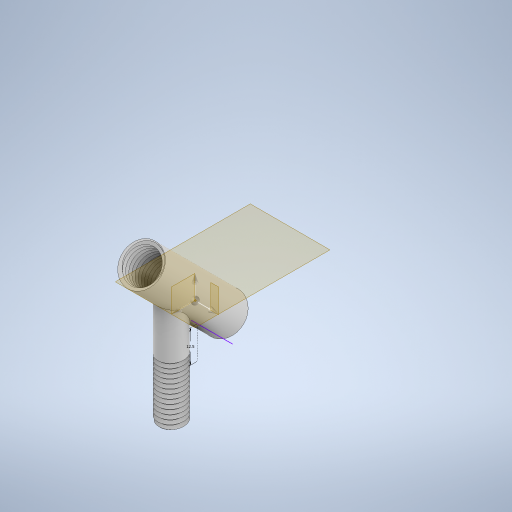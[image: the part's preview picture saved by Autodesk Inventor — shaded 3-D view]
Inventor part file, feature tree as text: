
AUTODESK INVENTOR PART (.ipt)
format: ipt  version: 2024 (Build 280153000, 153)  size: 883,200 bytes
history: native  units: mm
features: sketch x9, plane x5, extrude x3, helix x2, hole x1, chamfer x1
ambient origin geometry x8: Origin, YZ Plane, XZ Plane, XY Plane, X Axis, Y Axis, Z Axis, Center Point
bodies: Solid1 (feature_tree)
feature tree (21):
  extrude  "Extrusion1"  Depth=25.0mm TaperAngle=0.0deg
  plane  "Work Plane1"
  plane  "Work Plane3"
  sketch  "Sketch9"  dims[d16=10.0mm d17=12.5mm]
  plane  "Work Plane4"
  sketch  "Sketch10"  dims[d18=12.5mm d19=45.0deg]
  plane  "Work Plane5"
  extrude  "Extrusion4"  Depth=12.5mm
  hole  "Hole1"  [1 undecoded]
  extrude  "Extrusion5"  Depth=45.0mm TaperAngle=0.0deg
  chamfer  "Chamfer1"  Distance=25.0mm
  sketch  "Sketch14"  dims[d37=1.7mm]
  plane  "Work Plane6"
  helix  "Coil1"  [1 undecoded]
  helix  "Coil2"  [1 undecoded]
  sketch  "Sketch1"  dims[d0=10.0mm d1=25.0mm d2=0.0mm]
  sketch  "Sketch11"  dims[d20=15.0mm d21=45.0mm d22=0.0mm]
  sketch  "Sketch12"  dims[d23=12.0mm]
  sketch  "Sketch13"  dims[d24=12.0mm d25=6.0mm d26=4.0mm d27=2.0mm d28=90.0deg d29=8.0mm d30=20.594885mm d31=25.0mm d32=0.0mm d33=0.8mm d34=2.0mm d35=45.0deg d36=60.0deg]
  sketch  "Sketch15"  dims[d38=2.0mm]
  sketch  "Sketch16"  dims[d39=0.2mm d40=0.0mm d41=1.7mm d42=25.0mm d43=10.0mm d44=0.0mm d45=90.0deg d46=90.0deg d47=0.0mm d48=0.0mm d53=1.7mm d54=60.0deg d55=6.0mm d56=0.2mm d57=1.7mm d58=55.0mm d59=10.0mm d60=0.0mm d61=90.0deg d62=90.0deg d63=0.0mm d64=0.0mm]
note: 3 required parameter values undecoded (feature->parameter linkage not recoverable at this tier; creation-order binding heuristic only, values carry confidence <= 0.55)
